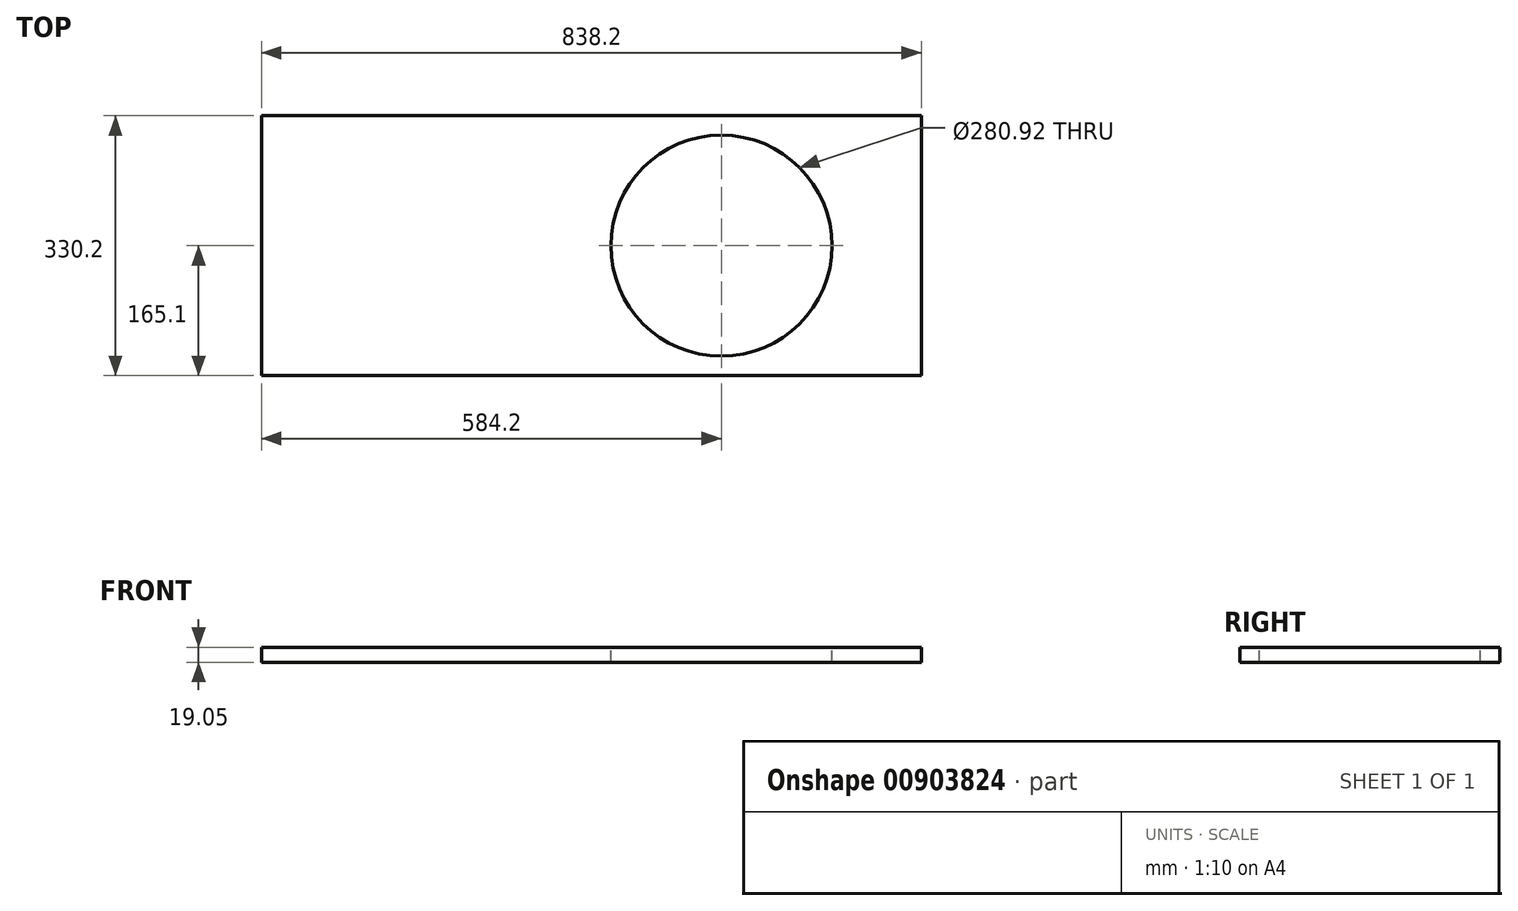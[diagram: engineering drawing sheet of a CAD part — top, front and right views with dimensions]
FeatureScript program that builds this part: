
annotation { "Feature Type Name" : "Feature", "Feature Type Description" : "" }
export const myFeature = defineFeature(function(context is Context, id is Id, definition is map)
    precondition{}
    {
        {
            var Q0;
            Q0=qCreatedBy(makeId("Top.planeOp"),FACE);
            var sketch = newSketch(context, id + "F0", { "sketchPlane" : qUnion([Q0])});
            skLineSegment(sketch, "E0.bottom", {"start": v(0, 0) * mm, "end": v(838.2, 0) * mm});
            skLineSegment(sketch, "E0.top", {"start": v(0, 330.2) * mm, "end": v(838.2, 330.2) * mm});
            skLineSegment(sketch, "E0.left", {"start": v(0, 0) * mm, "end": v(0, 330.2) * mm});
            skLineSegment(sketch, "E0.right", {"start": v(838.2, 0) * mm, "end": v(838.2, 330.2) * mm});
            skSolve(sketch);
        }
        {
            var Q0;
            Q0 = qSketchRegion(id + "F0", true);
            extrude(context, id + "F1", {"entities" : qUnion([Q0]), "depth" : 19.05 * mm, "offsetDistance" : 25.4 * mm});
        }
        {
            var Q0;
            Q0=makeQuery(id+"F1.opExtrude","CAP_FACE",FACE,{"disambiguationData":[OSD([sQuery(id+"F0.wireOp",EDGE,"E0.bottom"),sQuery(id+"F0.wireOp",EDGE,"E0.top"),sQuery(id+"F0.wireOp",EDGE,"E0.left"),sQuery(id+"F0.wireOp",EDGE,"E0.right")])],"isStart":false});
            var sketch = newSketch(context, id + "F2", { "sketchPlane" : qUnion([Q0])});
            skCircle(sketch, "E1", {"center": v(584.2, 165.1) * mm, "radius": 140.46 * mm});
            skLineSegment(sketch, "E2", {"start": v(838.2, 165.1) * mm, "end": v(0, 165.1) * mm, "construction": true});
            skSolve(sketch);
        }
        {
            var Q0;
            Q0 = qSketchRegion(id + "F2", true);
            extrude(context, id + "F3", {"entities" : qUnion([Q0]), "operationType" : NewBodyOperationType.REMOVE, "endBound" : BoundingType.THROUGH_ALL, "oppositeDirection" : true, "depth" : 25.4 * mm, "offsetDistance" : 25.4 * mm});
        }
    });
